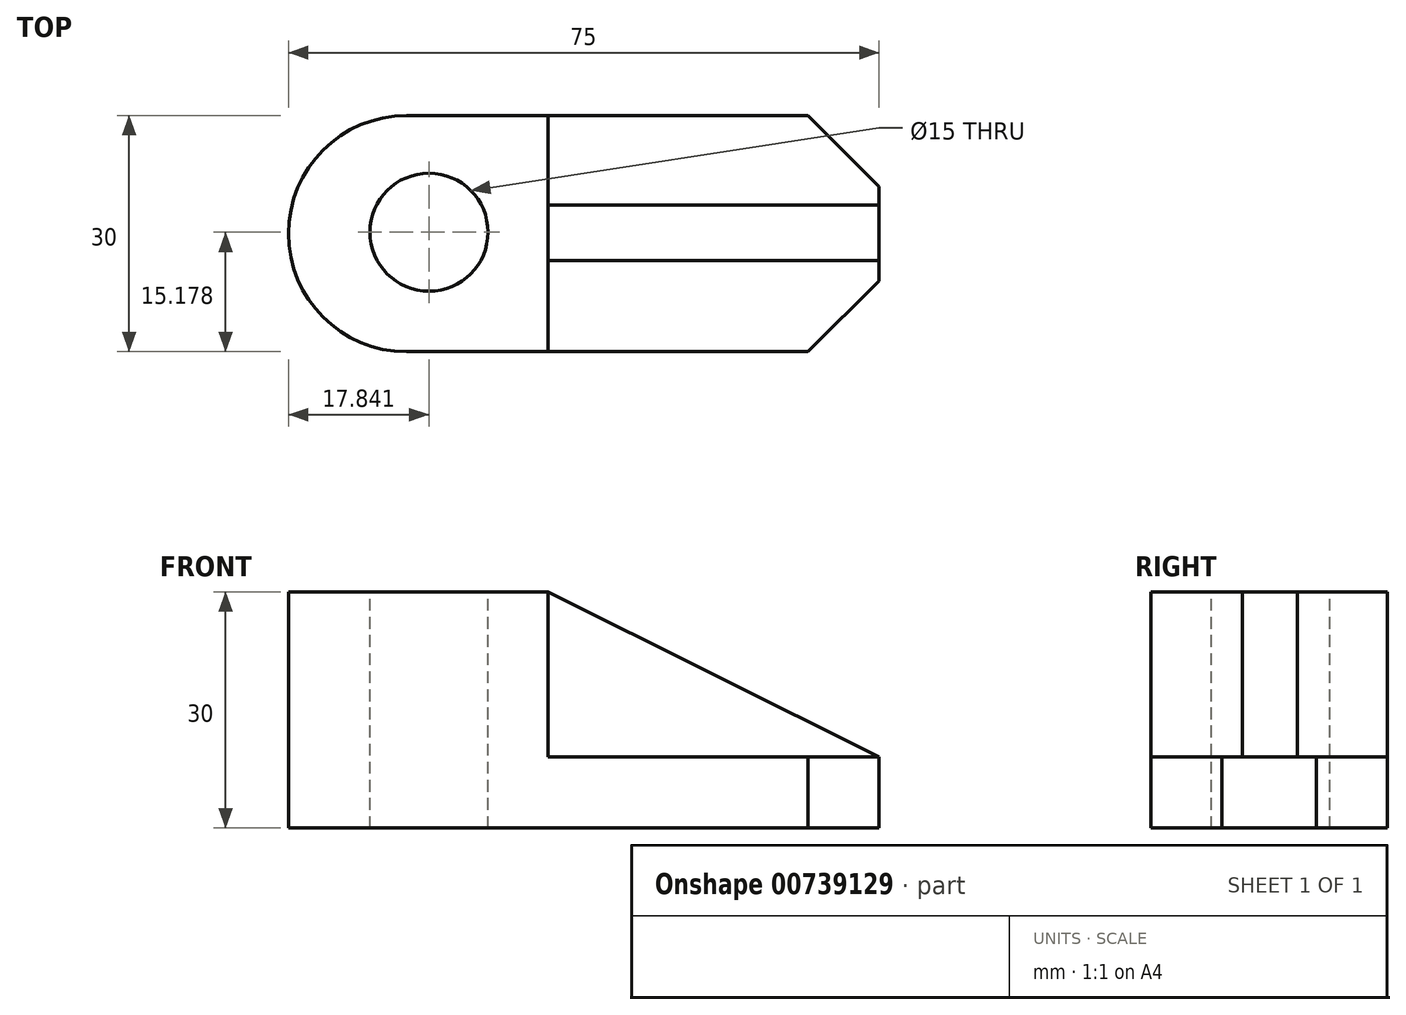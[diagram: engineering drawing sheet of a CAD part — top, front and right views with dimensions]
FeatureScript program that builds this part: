
annotation { "Feature Type Name" : "Feature", "Feature Type Description" : "" }
export const myFeature = defineFeature(function(context is Context, id is Id, definition is map)
    precondition{}
    {
        {
            var Q0;
            Q0=qCreatedBy(makeId("Top.planeOp"),FACE);
            var sketch = newSketch(context, id + "F0", { "sketchPlane" : qUnion([Q0])});
            skLineSegment(sketch, "E0", {"start": v(-3.16, 39.04) * mm, "end": v(-21.16, 39.04) * mm});
            skArc(sketch, "E1", {"start": v(-21.16, 39.04) * mm, "mid": v(-36.16, 24.04) * mm, "end": v(-21.16, 9.04) * mm});
            skLineSegment(sketch, "E2", {"start": v(-21.16, 9.04) * mm, "end": v(-3.16, 9.04) * mm});
            skLineSegment(sketch, "E3", {"start": v(-3.16, 39.04) * mm, "end": v(-3.16, 9.04) * mm});
            skSolve(sketch);
        }
        {
            var Q0;
            Q0 = qSketchRegion(id + "F0", true);
            extrude(context, id + "F1", {"entities" : qUnion([Q0]), "depth" : 30 * mm, "offsetDistance" : 25 * mm});
        }
        {
            var Q0;
            Q0=makeQuery(id+"F1.opExtrude","CAP_FACE",FACE,{"disambiguationData":[OSD([sQuery(id+"F0.wireOp",EDGE,"E0"),sQuery(id+"F0.wireOp",EDGE,"E1"),sQuery(id+"F0.wireOp",EDGE,"E2"),sQuery(id+"F0.wireOp",EDGE,"E3")])],"isStart":false});
            var sketch = newSketch(context, id + "F2", { "sketchPlane" : qUnion([Q0])});
            skCircle(sketch, "E4", {"center": v(-18.32, 24.22) * mm, "radius": 7.5 * mm});
            skSolve(sketch);
        }
        {
            var Q0;
            Q0 = qSketchRegion(id + "F2", true);
            extrude(context, id + "F3", {"entities" : qUnion([Q0]), "operationType" : NewBodyOperationType.REMOVE, "oppositeDirection" : true, "depth" : 30 * mm, "offsetDistance" : 25 * mm});
        }
        {
            var Q0;
            Q0=makeQuery(id+"F1.opExtrude","SWEPT_FACE",FACE,{"disambiguationData":[OSD([sQuery(id+"F0.wireOp",EDGE,"E3")])]});
            var sketch = newSketch(context, id + "F4", { "sketchPlane" : qUnion([Q0])});
            skLineSegment(sketch, "E5.bottom", {"start": v(39.04, 0) * mm, "end": v(9.04, 0) * mm});
            skLineSegment(sketch, "E5.top", {"start": v(39.04, 9) * mm, "end": v(9.04, 9) * mm});
            skLineSegment(sketch, "E5.left", {"start": v(39.04, 0) * mm, "end": v(39.04, 9) * mm});
            skLineSegment(sketch, "E5.right", {"start": v(9.04, 0) * mm, "end": v(9.04, 9) * mm});
            skSolve(sketch);
        }
        {
            var Q0;
            Q0 = qSketchRegion(id + "F4", true);
            extrude(context, id + "F5", {"entities" : qUnion([Q0]), "operationType" : NewBodyOperationType.ADD, "depth" : 42 * mm, "offsetDistance" : 25 * mm});
        }
        {
            var Q0;
            Q0=makeQuery(id+"F5.opExtrude","SWEPT_FACE",FACE,{"disambiguationData":[OSD([sQuery(id+"F4.wireOp",EDGE,"E5.top")])]});
            var sketch = newSketch(context, id + "F6", { "sketchPlane" : qUnion([Q0])});
            skLineSegment(sketch, "E6.bottom", {"start": v(38.84, 27.64) * mm, "end": v(-3.16, 27.64) * mm});
            skLineSegment(sketch, "E6.top", {"start": v(38.84, 20.64) * mm, "end": v(-3.16, 20.64) * mm});
            skLineSegment(sketch, "E6.left", {"start": v(38.84, 27.64) * mm, "end": v(38.84, 20.64) * mm});
            skLineSegment(sketch, "E6.right", {"start": v(-3.16, 27.64) * mm, "end": v(-3.16, 20.64) * mm});
            skSolve(sketch);
        }
        {
            var Q0;
            Q0 = qSketchRegion(id + "F6", true);
            extrude(context, id + "F7", {"entities" : qUnion([Q0]), "operationType" : NewBodyOperationType.ADD, "depth" : 21 * mm, "offsetDistance" : 25 * mm});
        }
        {
            var Q0;
            Q0=makeQuery(id+"F7.opExtrude","SWEPT_FACE",FACE,{"disambiguationData":[OSD([sQuery(id+"F6.wireOp",EDGE,"E6.top")])]});
            var sketch = newSketch(context, id + "F8", { "sketchPlane" : qUnion([Q0])});
            skLineSegment(sketch, "E7", {"start": v(-3.16, 30) * mm, "end": v(38.84, 9) * mm});
            skLineSegment(sketch, "E8", {"start": v(38.84, 9) * mm, "end": v(-3.16, 30) * mm});
            skLineSegment(sketch, "E9", {"start": v(-3.16, 30) * mm, "end": v(38.84, 30) * mm});
            skLineSegment(sketch, "E10", {"start": v(38.84, 30) * mm, "end": v(38.84, 9) * mm});
            skSolve(sketch);
        }
        {
            var Q0;
            Q0 = qSketchRegion(id + "F8", true);
            extrude(context, id + "F9", {"entities" : qUnion([Q0]), "operationType" : NewBodyOperationType.REMOVE, "oppositeDirection" : true, "depth" : 25 * mm, "offsetDistance" : 25 * mm});
        }
        {
            var Q0;
            {var subQ1=sQuery(id+"F4.wireOp",EDGE,"E5.top");Q0=makeQuery(id+"F7.boolean.opBoolean","SPLIT",FACE,{"disambiguationData":[TD([makeQuery(id+"F1.opExtrude","SWEPT_FACE",FACE,{"disambiguationData":[OSD([sQuery(id+"F0.wireOp",EDGE,"E0")])]})])],"derivedFrom":makeQuery(id+"F5.opExtrude","SWEPT_FACE",FACE,{"disambiguationData":[OSD([subQ1])]})});}
            var sketch = newSketch(context, id + "F10", { "sketchPlane" : qUnion([Q0])});
            skLineSegment(sketch, "E11", {"start": v(38.84, 39.04) * mm, "end": v(38.84, 30.04) * mm});
            skLineSegment(sketch, "E12", {"start": v(38.84, 30.04) * mm, "end": v(38.84, 39.04) * mm});
            skLineSegment(sketch, "E13", {"start": v(38.84, 39.04) * mm, "end": v(29.84, 39.04) * mm});
            skLineSegment(sketch, "E14", {"start": v(29.84, 39.04) * mm, "end": v(38.84, 30.04) * mm});
            skSolve(sketch);
        }
        {
            var Q0;
            Q0 = qSketchRegion(id + "F10", true);
            extrude(context, id + "F11", {"entities" : qUnion([Q0]), "operationType" : NewBodyOperationType.REMOVE, "oppositeDirection" : true, "depth" : 25 * mm, "offsetDistance" : 25 * mm});
        }
        {
            var Q0;
            {var subQ1=sQuery(id+"F4.wireOp",EDGE,"E5.top");Q0=makeQuery(id+"F7.boolean.opBoolean","SPLIT",FACE,{"disambiguationData":[TD([makeQuery(id+"F1.opExtrude","SWEPT_FACE",FACE,{"disambiguationData":[OSD([sQuery(id+"F0.wireOp",EDGE,"E2")])]})])],"derivedFrom":makeQuery(id+"F5.opExtrude","SWEPT_FACE",FACE,{"disambiguationData":[OSD([subQ1])]})});}
            var sketch = newSketch(context, id + "F12", { "sketchPlane" : qUnion([Q0])});
            skLineSegment(sketch, "E15", {"start": v(38.84, 9.04) * mm, "end": v(38.84, 18.04) * mm});
            skLineSegment(sketch, "E16", {"start": v(38.84, 9.04) * mm, "end": v(29.84, 9.04) * mm});
            skLineSegment(sketch, "E17", {"start": v(29.84, 9.04) * mm, "end": v(38.84, 18.04) * mm});
            skSolve(sketch);
        }
        {
            var Q0;
            Q0 = qSketchRegion(id + "F12", true);
            extrude(context, id + "F13", {"entities" : qUnion([Q0]), "operationType" : NewBodyOperationType.REMOVE, "oppositeDirection" : true, "depth" : 25 * mm, "offsetDistance" : 25 * mm});
        }
    });
